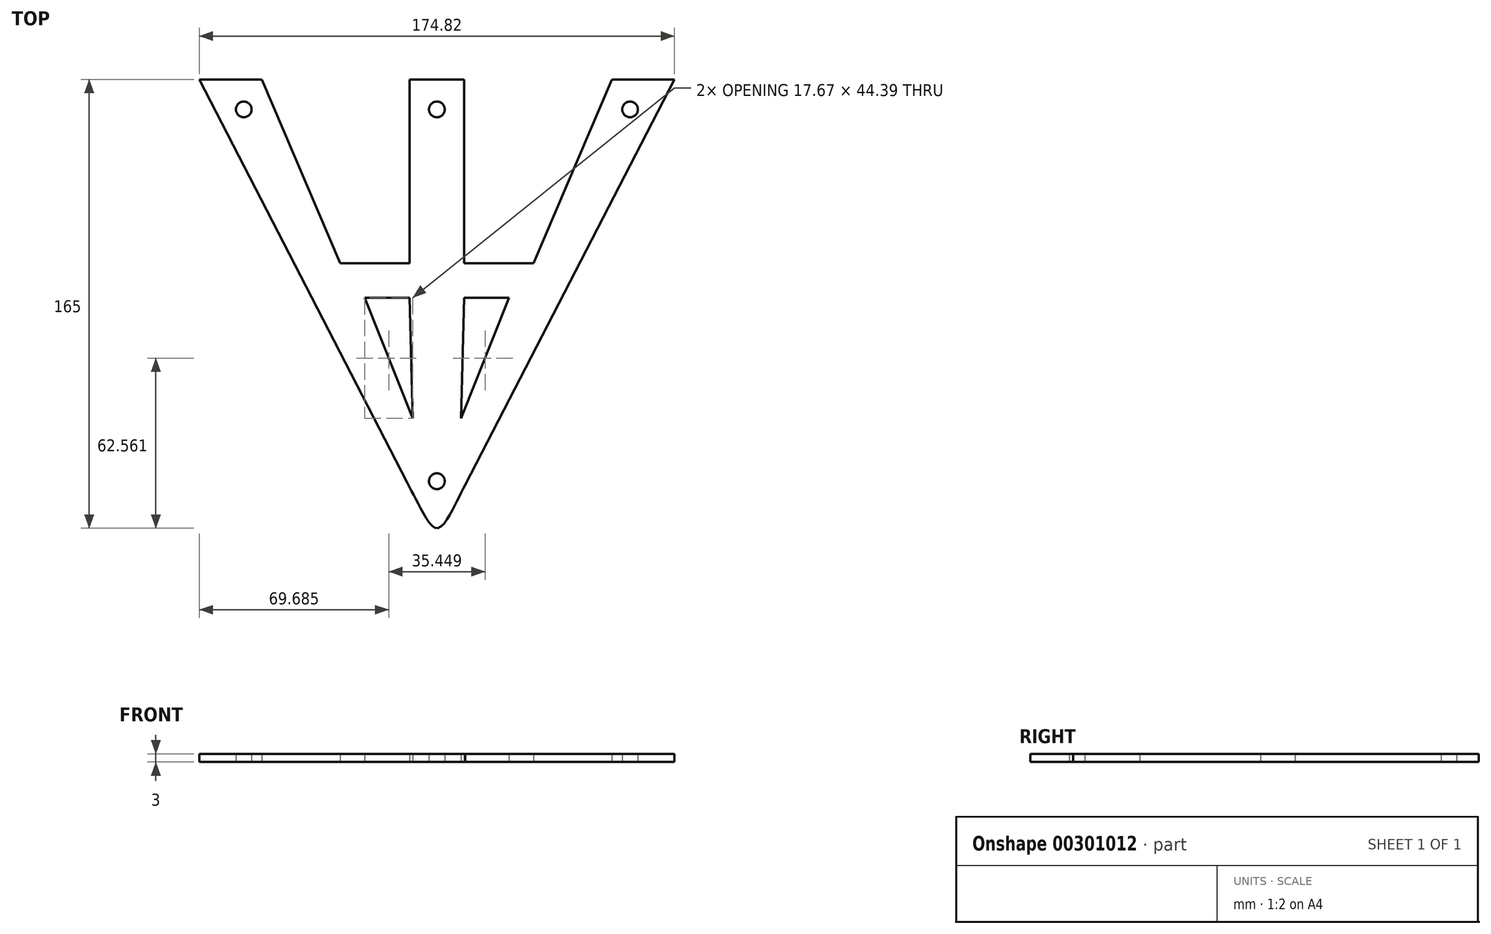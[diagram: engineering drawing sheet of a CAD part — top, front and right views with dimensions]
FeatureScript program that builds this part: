
annotation { "Feature Type Name" : "Feature", "Feature Type Description" : "" }
export const myFeature = defineFeature(function(context is Context, id is Id, definition is map)
    precondition{}
    {
        {
            var Q0;
            Q0=qCreatedBy(makeId("Top.planeOp"),FACE);
            var sketch = newSketch(context, id + "F0", { "sketchPlane" : qUnion([Q0])});
            skLineSegment(sketch, "E0", {"start": v(0, -87.19) * mm, "end": v(-87.41, 82.12) * mm, "construction": true});
            skLineSegment(sketch, "E1", {"start": v(-87.41, 82.12) * mm, "end": v(87.41, 82.12) * mm, "construction": true});
            skLineSegment(sketch, "E2", {"start": v(87.41, 82.12) * mm, "end": v(0, -87.19) * mm, "construction": true});
            skFitSpline(sketch, "E3", {"points": [v(10.41, -67.02) * mm, v(5.85, -75.86) * mm, v(0, -82.88) * mm, v(-5.96, -75.65) * mm, v(-10.91, -66.05) * mm], "startDerivative": vector(-17.01, -32.05) * mm, "endDerivative": vector(-17.8, 34.85) * mm});
            skLineSegment(sketch, "E4", {"start": v(10.41, -67.02) * mm, "end": v(87.41, 82.12) * mm});
            skLineSegment(sketch, "E5", {"start": v(-10.91, -66.05) * mm, "end": v(-87.41, 82.12) * mm});
            skPoint(sketch, "E6", {"position": v(0, 82.12) * mm});
            skLineSegment(sketch, "E7", {"start": v(87.41, 82.12) * mm, "end": v(64.37, 82.12) * mm});
            skLineSegment(sketch, "E8", {"start": v(0, 82.12) * mm, "end": v(10.04, 82.12) * mm});
            skLineSegment(sketch, "E9", {"start": v(10.04, 82.12) * mm, "end": v(10.04, 14.57) * mm});
            skLineSegment(sketch, "E10", {"start": v(10.04, 1.88) * mm, "end": v(26.56, 1.88) * mm});
            skLineSegment(sketch, "E11", {"start": v(8.89, -42.51) * mm, "end": v(26.56, 1.88) * mm});
            skLineSegment(sketch, "E12", {"start": v(35.53, 14.57) * mm, "end": v(64.37, 82.12) * mm});
            skLineSegment(sketch, "E13", {"start": v(35.53, 14.57) * mm, "end": v(10.04, 14.57) * mm});
            skLineSegment(sketch, "E14.MirrorCS", {"start": v(-8.89, -42.51) * mm, "end": v(-26.56, 1.88) * mm});
            skLineSegment(sketch, "E15.MirrorCS", {"start": v(-10.04, 1.88) * mm, "end": v(-26.56, 1.88) * mm});
            skLineSegment(sketch, "E16.MirrorCS", {"start": v(-35.53, 14.57) * mm, "end": v(-10.04, 14.57) * mm});
            skLineSegment(sketch, "E17.MirrorCS", {"start": v(-10.04, 82.12) * mm, "end": v(-10.04, 14.57) * mm});
            skLineSegment(sketch, "E18.MirrorCS", {"start": v(-35.53, 14.57) * mm, "end": v(-64.37, 82.12) * mm});
            skLineSegment(sketch, "E19.MirrorCS", {"start": v(0, 82.12) * mm, "end": v(-10.04, 82.12) * mm});
            skLineSegment(sketch, "E20", {"start": v(-87.41, 82.12) * mm, "end": v(-64.37, 82.12) * mm});
            skLineSegment(sketch, "E21", {"start": v(8.89, -42.51) * mm, "end": v(10.04, 1.88) * mm});
            skLineSegment(sketch, "E22", {"start": v(-8.89, -42.51) * mm, "end": v(-10.04, 1.88) * mm});
            skSolve(sketch);
        }
        {
            var Q0;
            Q0=makeQuery(id+"F0.imprint","IMPRINT",FACE,{"disambiguationData":[TD([[makeQuery(id+"F0.imprint","IMPRINT",EDGE,{"derivedFrom":sQuery(id+"F0.wireOp",EDGE,"E3")}),-1.0]])]});
            extrude(context, id + "F1", {"entities" : qUnion([Q0]), "depth" : 3 * mm, "offsetDistance" : 25 * mm});
        }
        {
            var Q0;
            Q0=qCreatedBy(makeId("Top.planeOp"),FACE);
            var sketch = newSketch(context, id + "F2", { "sketchPlane" : qUnion([Q0])});
            skLineSegment(sketch, "E23", {"start": v(-11.44, -65.6) * mm, "end": v(11.39, -65.6) * mm, "construction": true});
            skPoint(sketch, "E24", {"position": v(0, -65.6) * mm});
            skSolve(sketch);
        }
        {
            var Q0;
            Q0=qCreatedBy(makeId("Top.planeOp"),FACE);
            var sketch = newSketch(context, id + "F3", { "sketchPlane" : qUnion([Q0])});
            skLineSegment(sketch, "E25", {"start": v(0, -64.88) * mm, "end": v(0, 207.16) * mm, "construction": true});
            skLineSegment(sketch, "E26", {"start": v(0, 71.14) * mm, "end": v(-71.06, 71.14) * mm, "construction": true});
            skLineSegment(sketch, "E27", {"start": v(-56.97, 71.14) * mm, "end": v(-56.97, -32.3) * mm, "construction": true});
            skLineSegment(sketch, "E28", {"start": v(-56.97, -32.3) * mm, "end": v(-56.97, 8.94) * mm, "construction": true});
            skLineSegment(sketch, "E29.MirrorCS", {"start": v(56.97, -32.3) * mm, "end": v(56.97, 8.94) * mm, "construction": true});
            skLineSegment(sketch, "E30.MirrorCS", {"start": v(0, 71.14) * mm, "end": v(71.06, 71.14) * mm, "construction": true});
            skPoint(sketch, "E31", {"position": v(56.97, 71.14) * mm});
            skSolve(sketch);
        }
        {
            var Q0;
            Q0=sQuery(id+"F3.wireOp",VERTEX,"E26.end");
            var Q1;
            Q1=sQuery(id+"F3.wireOp",VERTEX,"E30.MirrorCS.start");
            var Q2;
            Q2=sQuery(id+"F3.wireOp",VERTEX,"E30.MirrorCS.end");
            var Q3;
            Q3=sQuery(id+"F2.wireOp",VERTEX,"E24");
            var Q4;
            Q4=makeQuery(id+"F1.opExtrude","SWEPT_BODY",BODY,{"disambiguationData":[OSD([sQuery(id+"F0.wireOp",EDGE,"E3"),sQuery(id+"F0.wireOp",EDGE,"E4"),sQuery(id+"F0.wireOp",EDGE,"E5"),sQuery(id+"F0.wireOp",EDGE,"E7"),sQuery(id+"F0.wireOp",EDGE,"E8"),sQuery(id+"F0.wireOp",EDGE,"E9"),sQuery(id+"F0.wireOp",EDGE,"E10"),sQuery(id+"F0.wireOp",EDGE,"E11"),sQuery(id+"F0.wireOp",EDGE,"E12"),sQuery(id+"F0.wireOp",EDGE,"E13"),sQuery(id+"F0.wireOp",EDGE,"E14.MirrorCS"),sQuery(id+"F0.wireOp",EDGE,"E15.MirrorCS"),sQuery(id+"F0.wireOp",EDGE,"E16.MirrorCS"),sQuery(id+"F0.wireOp",EDGE,"E17.MirrorCS"),sQuery(id+"F0.wireOp",EDGE,"E18.MirrorCS"),sQuery(id+"F0.wireOp",EDGE,"E19.MirrorCS"),sQuery(id+"F0.wireOp",EDGE,"E20"),sQuery(id+"F0.wireOp",EDGE,"E21"),sQuery(id+"F0.wireOp",EDGE,"E22")])]});
            hole(context, id + "F4", {"style" : HoleStyle.SIMPLE, "endStyle" : HoleEndStyle.THROUGH, "oppositeDirection" : true, "holeDiameter" : 5.8 * mm, "majorDiameter" : 5 * mm, "isTappedThrough" : true, "tappedDepth" : 12 * mm, "tapClearance" : 3, "locations" : qUnion([Q0, Q1, Q2, Q3]), "scope" : qUnion([Q4])});
        }
    });
